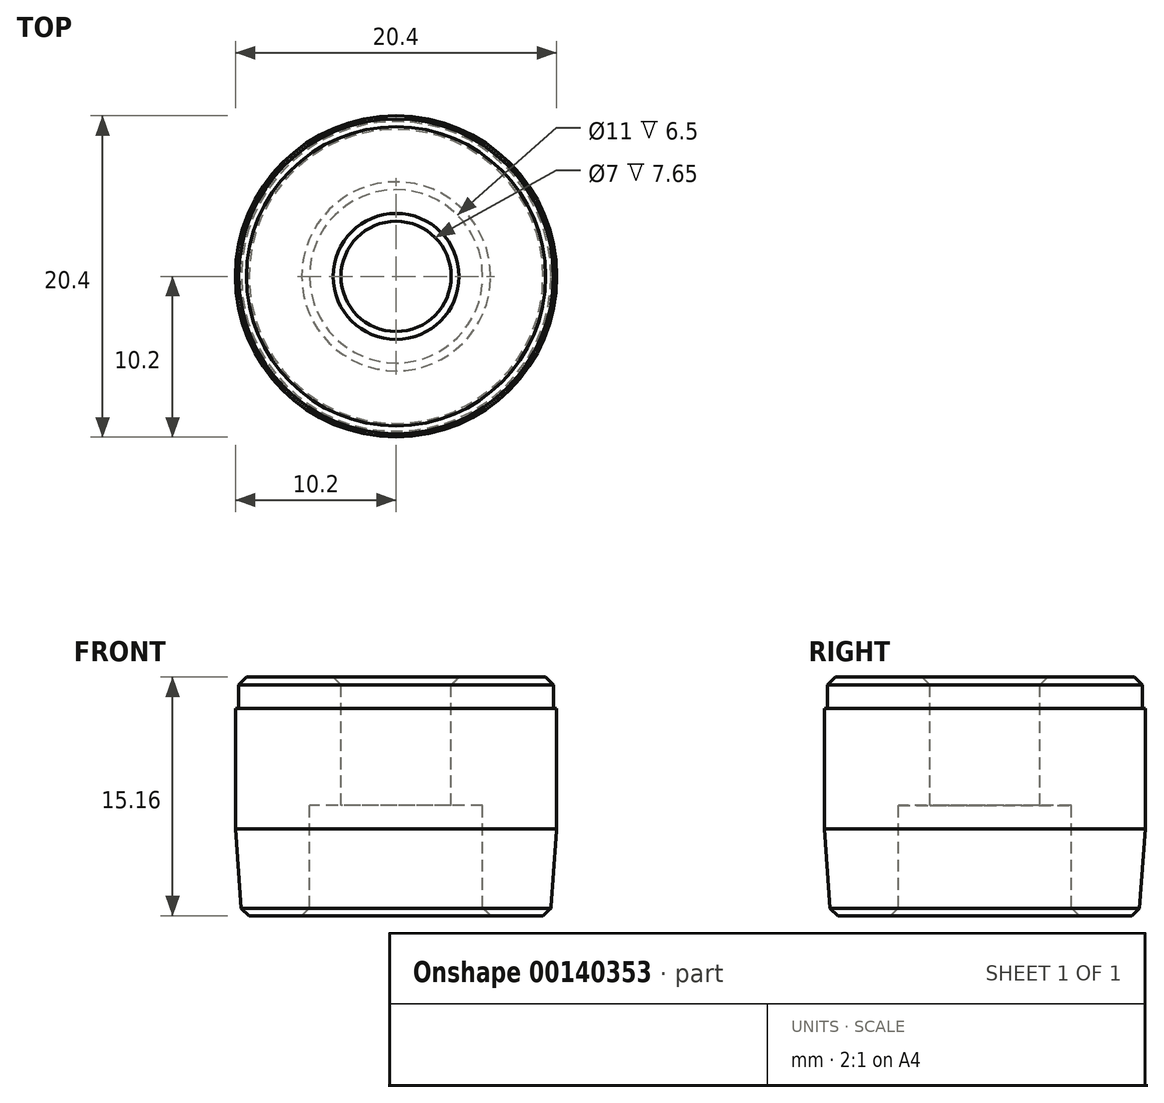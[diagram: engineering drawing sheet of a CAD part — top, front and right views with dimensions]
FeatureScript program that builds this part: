
annotation { "Feature Type Name" : "Feature", "Feature Type Description" : "" }
export const myFeature = defineFeature(function(context is Context, id is Id, definition is map)
    precondition{}
    {
        {
            var Q0;
            Q0=qCreatedBy(makeId("Front.planeOp"),FACE);
            var sketch = newSketch(context, id + "F0", { "sketchPlane" : qUnion([Q0])});
            skLineSegment(sketch, "E0.bottom", {"start": v(10, 7.58) * mm, "end": v(-10, 7.58) * mm});
            skLineSegment(sketch, "E0.top", {"start": v(9.8, -7.57) * mm, "end": v(-9.8, -7.57) * mm});
            skLineSegment(sketch, "E0.left", {"start": v(10.2, 5.58) * mm, "end": v(10.2, -2.07) * mm});
            skLineSegment(sketch, "E0.right", {"start": v(-10.2, 5.58) * mm, "end": v(-10.2, -2.07) * mm});
            skPoint(sketch, "E0.middle", {"position": v(0, 0) * mm});
            skLineSegment(sketch, "E1", {"start": v(0, 13.27) * mm, "end": v(0, -12.53) * mm, "construction": true});
            skLineSegment(sketch, "E2", {"start": v(-10, 7.58) * mm, "end": v(-10, 5.58) * mm});
            skLineSegment(sketch, "E3", {"start": v(-10, 5.58) * mm, "end": v(-10.2, 5.58) * mm});
            skLineSegment(sketch, "E4.MirrorCS", {"start": v(10, 5.58) * mm, "end": v(10.2, 5.58) * mm});
            skLineSegment(sketch, "E5.MirrorCS", {"start": v(10, 7.58) * mm, "end": v(10, 5.58) * mm});
            skLineSegment(sketch, "E6.bottom", {"start": v(3.5, 7.58) * mm, "end": v(-3.5, 7.58) * mm});
            skLineSegment(sketch, "E6.top", {"start": v(3.5, -7.58) * mm, "end": v(-3.5, -7.58) * mm});
            skLineSegment(sketch, "E6.left", {"start": v(3.5, 7.58) * mm, "end": v(3.5, -0.57) * mm});
            skLineSegment(sketch, "E6.right", {"start": v(-3.5, 7.58) * mm, "end": v(-3.5, -0.57) * mm});
            skLineSegment(sketch, "E7", {"start": v(-3.5, -0.57) * mm, "end": v(-5.5, -0.57) * mm});
            skLineSegment(sketch, "E8", {"start": v(-5.5, -0.57) * mm, "end": v(-5.5, -7.57) * mm});
            skLineSegment(sketch, "E9.MirrorCS", {"start": v(5.5, -0.57) * mm, "end": v(5.5, -7.57) * mm});
            skLineSegment(sketch, "E10.MirrorCS", {"start": v(3.5, -0.57) * mm, "end": v(5.5, -0.57) * mm});
            skPoint(sketch, "E11.orphan", {"position": v(10.2, 7.58) * mm});
            skPoint(sketch, "E12.orphan", {"position": v(-10.2, 7.58) * mm});
            skLineSegment(sketch, "E13", {"start": v(-10.2, -2.07) * mm, "end": v(-9.8, -7.57) * mm});
            skLineSegment(sketch, "E14.MirrorCS", {"start": v(10.2, -2.07) * mm, "end": v(9.8, -7.57) * mm});
            skPoint(sketch, "E15.orphan", {"position": v(-10.2, -7.57) * mm});
            skPoint(sketch, "E16.orphan", {"position": v(10.2, -7.57) * mm});
            skSolve(sketch);
        }
        {
            var Q0;
            Q0=makeQuery(id+"F0.imprint","IMPRINT",FACE,{"disambiguationData":[TD([[makeQuery(id+"F0.imprint","IMPRINT",EDGE,{"derivedFrom":sQuery(id+"F0.wireOp",EDGE,"E0.right")}),1.0]])]});
            var Q1;
            Q1=sQuery(id+"F0.wireOp",EDGE,"E1");
            revolve(context, id + "F1", {"entities" : qUnion([Q0]), "axis" : qUnion([Q1]), "revolveType" : RevolveType.FULL});
        }
        {
            var Q0;
            Q0=makeQuery(id+"F1.opRevolve","SWEPT_EDGE",EDGE,{"disambiguationData":[OSD([sQuery(id+"F0.wireOp",EDGE,"E0.top"),sQuery(id+"F0.wireOp",EDGE,"E8")])]});
            var Q1;
            Q1=makeQuery(id+"F1.opRevolve","SWEPT_EDGE",EDGE,{"disambiguationData":[OSD([sQuery(id+"F0.wireOp",EDGE,"E0.top"),sQuery(id+"F0.wireOp",EDGE,"E13")])]});
            var Q2;
            Q2=makeQuery(id+"F1.opRevolve","SWEPT_EDGE",EDGE,{"disambiguationData":[OSD([sQuery(id+"F0.wireOp",EDGE,"E0.bottom"),sQuery(id+"F0.wireOp",EDGE,"E2")])]});
            var Q3;
            Q3=makeQuery(id+"F1.opRevolve","SWEPT_EDGE",EDGE,{"disambiguationData":[OSD([sQuery(id+"F0.wireOp",EDGE,"E0.bottom"),sQuery(id+"F0.wireOp",EDGE,"E6.bottom"),sQuery(id+"F0.wireOp",EDGE,"E6.right")])]});
            chamfer(context, id + "F2", {"entities" : qUnion([Q0, Q1, Q2, Q3]), "width" : 0.5 * mm, "tangentPropagation" : true});
        }
    });
